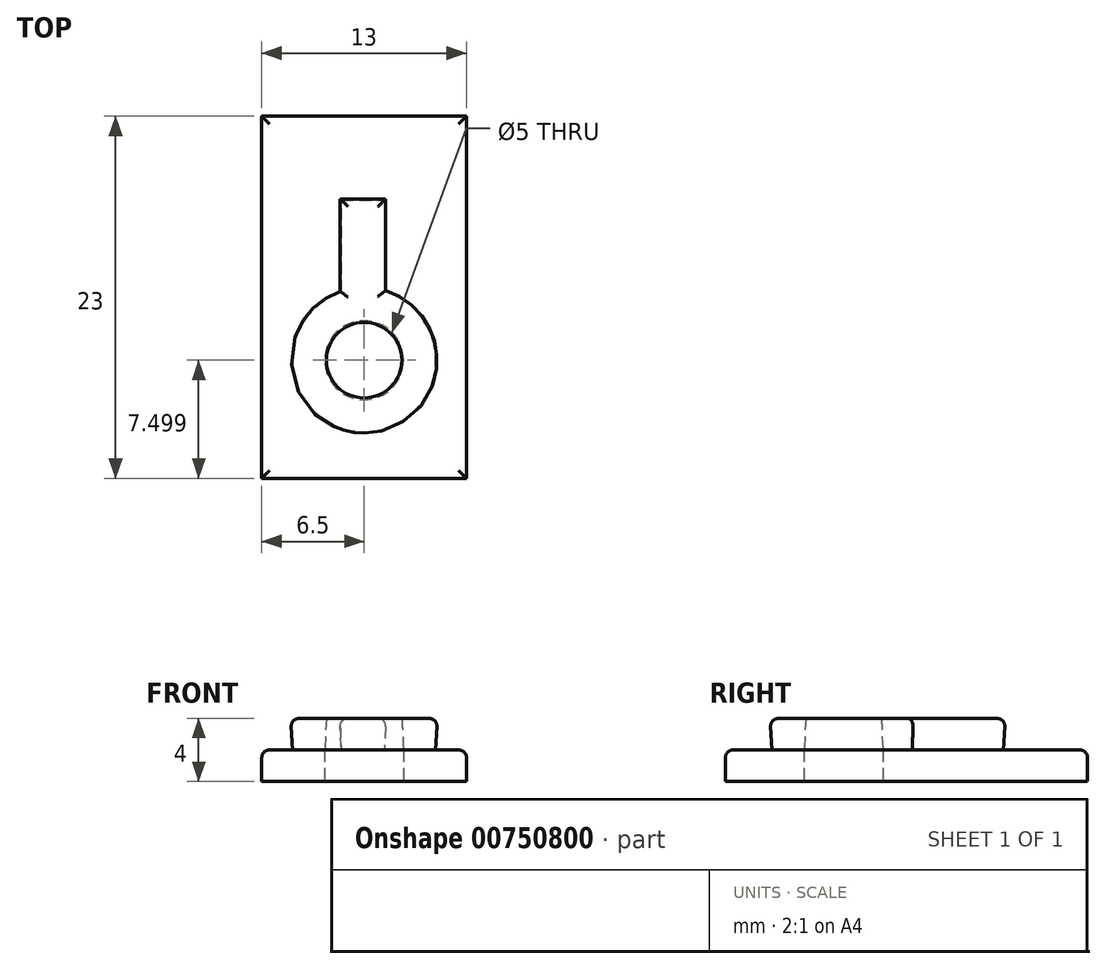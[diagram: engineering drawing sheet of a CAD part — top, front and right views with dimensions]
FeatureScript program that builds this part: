
annotation { "Feature Type Name" : "Feature", "Feature Type Description" : "" }
export const myFeature = defineFeature(function(context is Context, id is Id, definition is map)
    precondition{}
    {
        {
            var Q0;
            Q0=qCreatedBy(makeId("Top.planeOp"),FACE);
            var sketch = newSketch(context, id + "F0", { "sketchPlane" : qUnion([Q0])});
            skLineSegment(sketch, "E0.bottom", {"start": v(-6.5, 42.07) * mm, "end": v(6.5, 42.07) * mm});
            skLineSegment(sketch, "E0.top", {"start": v(-6.5, 19.07) * mm, "end": v(6.5, 19.07) * mm});
            skLineSegment(sketch, "E0.left", {"start": v(-6.5, 42.07) * mm, "end": v(-6.5, 19.07) * mm});
            skLineSegment(sketch, "E0.right", {"start": v(6.5, 42.07) * mm, "end": v(6.5, 19.07) * mm});
            skPoint(sketch, "E1", {"position": v(0, 26.57) * mm});
            skCircle(sketch, "E2", {"center": v(0, 26.57) * mm, "radius": 2.5 * mm});
            skSolve(sketch);
        }
        {
            var Q0;
            Q0=makeQuery(id+"F0.imprint","IMPRINT",FACE,{"disambiguationData":[TD([[makeQuery(id+"F0.imprint","IMPRINT",EDGE,{"derivedFrom":sQuery(id+"F0.wireOp",EDGE,"E0.bottom")}),-1.0]])]});
            extrude(context, id + "F1", {"entities" : qUnion([Q0]), "depth" : 2 * mm, "offsetDistance" : 25.4 * mm});
        }
        {
            var Q0;
            Q0=makeQuery(id+"F1.opExtrude","CAP_FACE",FACE,{"disambiguationData":[OSD([sQuery(id+"F0.wireOp",EDGE,"E0.bottom"),sQuery(id+"F0.wireOp",EDGE,"E0.top"),sQuery(id+"F0.wireOp",EDGE,"E0.left"),sQuery(id+"F0.wireOp",EDGE,"E0.right"),sQuery(id+"F0.wireOp",EDGE,"E2")])],"isStart":false});
            var sketch = newSketch(context, id + "F2", { "sketchPlane" : qUnion([Q0])});
            skCircle(sketch, "E3", {"center": v(0, 26.57) * mm, "radius": 4.55 * mm});
            skLineSegment(sketch, "E4.bottom", {"start": v(-1.44, 36.74) * mm, "end": v(1.29, 36.74) * mm});
            skLineSegment(sketch, "E4.top", {"start": v(-1.44, 28.71) * mm, "end": v(1.29, 28.71) * mm});
            skLineSegment(sketch, "E4.left", {"start": v(-1.44, 36.74) * mm, "end": v(-1.44, 28.71) * mm});
            skLineSegment(sketch, "E4.right", {"start": v(1.29, 36.74) * mm, "end": v(1.29, 28.71) * mm});
            skSolve(sketch);
        }
        {
            var Q0;
            {var subQ0=sQuery(id+"F2.wireOp",EDGE,"E4.left");var subQ3=sQuery(id+"F2.wireOp",EDGE,"E3");var subQ4=makeQuery(id+"F2.imprint","INTERSECT",VERTEX,{"derivedFrom":[subQ3,subQ0]});Q0=makeQuery(id+"F2.imprint","IMPRINT",FACE,{"disambiguationData":[TD([[makeQuery(id+"F2.imprint","IMPRINT",EDGE,{"disambiguationData":[TD([[subQ4,1.0]])],"derivedFrom":subQ3}),1.0]])]});}
            var Q1;
            {var subQ5=sQuery(id+"F2.wireOp",EDGE,"E4.bottom");Q1=makeQuery(id+"F2.imprint","IMPRINT",FACE,{"disambiguationData":[TD([[makeQuery(id+"F2.imprint","IMPRINT",EDGE,{"derivedFrom":subQ5}),-1.0]])]});}
            var Q2;
            {var subQ4=sQuery(id+"F2.wireOp",EDGE,"E3");var subQ6=sQuery(id+"F2.wireOp",EDGE,"E4.left");var subQ9=makeQuery(id+"F2.imprint","INTERSECT",VERTEX,{"derivedFrom":[subQ4,subQ6]});Q2=makeQuery(id+"F2.imprint","IMPRINT",FACE,{"disambiguationData":[TD([[makeQuery(id+"F2.imprint","IMPRINT",EDGE,{"disambiguationData":[TD([[subQ9,-1.0]])],"derivedFrom":subQ4}),1.0]])]});}
            extrude(context, id + "F3", {"entities" : qUnion([Q0, Q1, Q2]), "operationType" : NewBodyOperationType.ADD, "depth" : 2 * mm, "offsetDistance" : 25.4 * mm, "hasDraft" : true, "draftAngle" : 3 * degree});
        }
        {
            var Q0;
            Q0=makeQuery(id+"F1.opExtrude","CAP_EDGE",EDGE,{"disambiguationData":[OSD([sQuery(id+"F0.wireOp",EDGE,"E0.right")])],"isStart":false});
            var Q1;
            Q1=makeQuery(id+"F3.opExtrude","CAP_EDGE",EDGE,{"disambiguationData":[OSD([sQuery(id+"F2.wireOp",EDGE,"E3")])],"isStart":false});
            var Q2;
            Q2=makeQuery(id+"F3.opExtrude","CAP_EDGE",EDGE,{"disambiguationData":[OSD([sQuery(id+"F2.wireOp",EDGE,"E4.right")])],"isStart":false});
            var Q3;
            Q3=makeQuery(id+"F3.opExtrude","CAP_EDGE",EDGE,{"disambiguationData":[OSD([sQuery(id+"F2.wireOp",EDGE,"E4.left")])],"isStart":false});
            var Q4;
            Q4=makeQuery(id+"F3.opExtrude","CAP_EDGE",EDGE,{"disambiguationData":[OSD([sQuery(id+"F2.wireOp",EDGE,"E4.bottom")])],"isStart":false});
            var Q5;
            Q5=makeQuery(id+"F1.opExtrude","CAP_EDGE",EDGE,{"disambiguationData":[OSD([sQuery(id+"F0.wireOp",EDGE,"E0.top")])],"isStart":false});
            var Q6;
            Q6=makeQuery(id+"F1.opExtrude","CAP_EDGE",EDGE,{"disambiguationData":[OSD([sQuery(id+"F0.wireOp",EDGE,"E0.left")])],"isStart":false});
            var Q7;
            Q7=makeQuery(id+"F1.opExtrude","CAP_EDGE",EDGE,{"disambiguationData":[OSD([sQuery(id+"F0.wireOp",EDGE,"E0.bottom")])],"isStart":false});
            fillet(context, id + "F4", {"entities" : qUnion([Q0, Q1, Q2, Q3, Q4, Q5, Q6, Q7]), "radius" : .5 * mm, "tangentPropagation" : true, "allowEdgeOverflow" : false});
        }
    });
